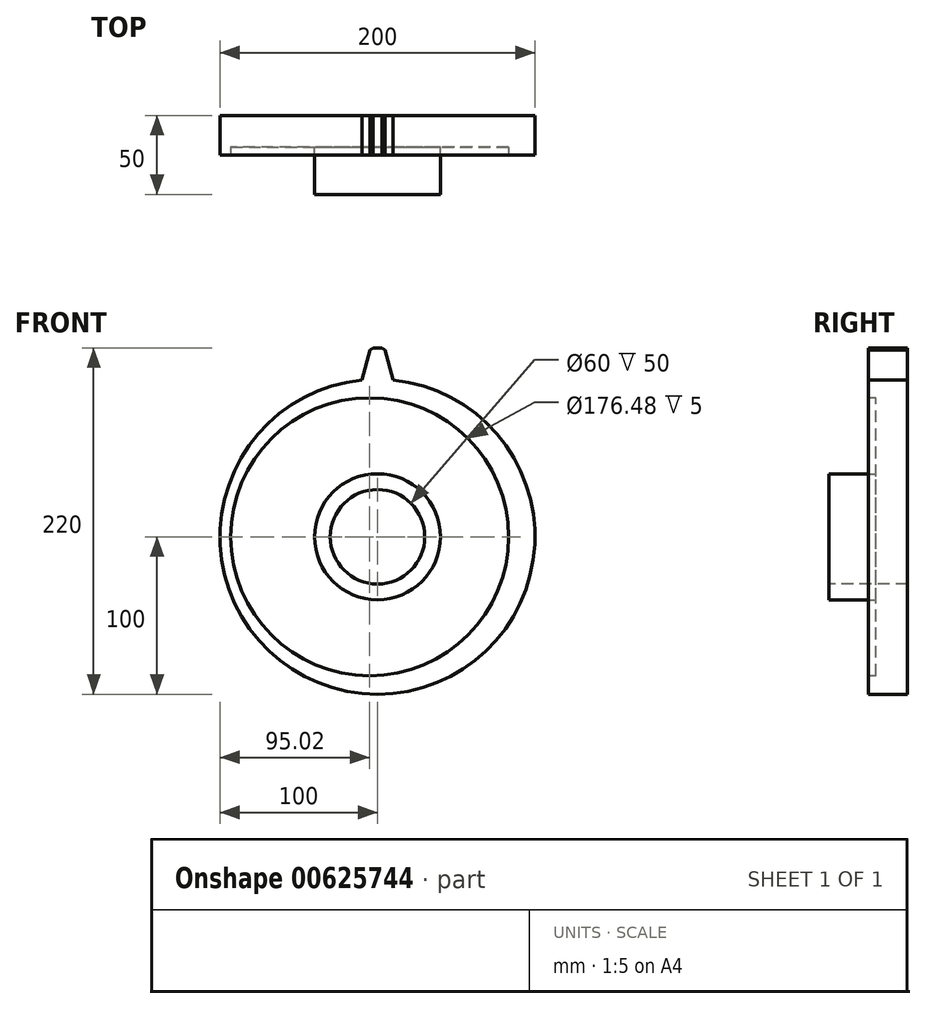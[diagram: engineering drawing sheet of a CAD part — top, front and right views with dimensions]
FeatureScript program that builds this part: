
annotation { "Feature Type Name" : "Feature", "Feature Type Description" : "" }
export const myFeature = defineFeature(function(context is Context, id is Id, definition is map)
    precondition{}
    {
        {
            var Q0;
            Q0=qCreatedBy(makeId("Front.planeOp"),FACE);
            var sketch = newSketch(context, id + "F0", { "sketchPlane" : qUnion([Q0])});
            skCircle(sketch, "E0", {"center": v(0, 0) * mm, "radius": 100 * mm});
            skSolve(sketch);
        }
        {
            var Q0;
            Q0 = qSketchRegion(id + "F0", true);
            extrude(context, id + "F1", {"entities" : qUnion([Q0]), "depth" : 25 * mm, "offsetDistance" : 25 * mm});
        }
        {
            var Q0;
            Q0=makeQuery(id+"F1.opExtrude","CAP_FACE",FACE,{"disambiguationData":[OSD([sQuery(id+"F0.wireOp",EDGE,"E0")])],"isStart":false});
            var sketch = newSketch(context, id + "F2", { "sketchPlane" : qUnion([Q0])});
            skLineSegment(sketch, "E1", {"start": v(-4.5, 120) * mm, "end": v(4.5, 120) * mm});
            skLineSegment(sketch, "E2", {"start": v(4.5, 120) * mm, "end": v(10, 99.5) * mm});
            skLineSegment(sketch, "E3", {"start": v(-4.5, 120) * mm, "end": v(-10, 99.5) * mm});
            skLineSegment(sketch, "E4", {"start": v(10, 99.5) * mm, "end": v(-10, 99.5) * mm});
            skSolve(sketch);
        }
        {
            var Q0;
            Q0 = qSketchRegion(id + "F2", true);
            extrude(context, id + "F3", {"entities" : qUnion([Q0]), "operationType" : NewBodyOperationType.ADD, "oppositeDirection" : true, "depth" : 25 * mm, "offsetDistance" : 25 * mm});
        }
        {
            var Q0;
            Q0=makeQuery(id+"F3.opExtrude","SWEPT_EDGE",EDGE,{"disambiguationData":[OSD([sQuery(id+"F2.wireOp",EDGE,"E1"),sQuery(id+"F2.wireOp",EDGE,"E2")])]});
            var Q1;
            Q1=makeQuery(id+"F3.opExtrude","SWEPT_EDGE",EDGE,{"disambiguationData":[OSD([sQuery(id+"F2.wireOp",EDGE,"E1"),sQuery(id+"F2.wireOp",EDGE,"E3")])]});
            chamfer(context, id + "F4", {"entities" : qUnion([Q0, Q1]), "width" : 2 * mm, "tangentPropagation" : true});
        }
        {
            var Q0;
            Q0=makeQuery(id+"F3.opExtrude","SWEPT_EDGE",EDGE,{"disambiguationData":[OSD([sQuery(id+"F0.wireOp",EDGE,"E0"),sQuery(id+"F2.wireOp",EDGE,"E2"),sQuery(id+"F2.wireOp",EDGE,"E4")])]});
            var Q1;
            Q1=makeQuery(id+"F3.opExtrude","SWEPT_EDGE",EDGE,{"disambiguationData":[OSD([sQuery(id+"F0.wireOp",EDGE,"E0"),sQuery(id+"F2.wireOp",EDGE,"E3"),sQuery(id+"F2.wireOp",EDGE,"E4")])]});
            fillet(context, id + "F5", {"entities" : qUnion([Q0, Q1]), "radius" : 5 * mm, "tangentPropagation" : true, "allowEdgeOverflow" : false});
        }
        {
            var Q0;
            {var subQ0=sQuery(id+"F2.wireOp",EDGE,"E4");var subQ1=sQuery(id+"F2.wireOp",EDGE,"E3");var subQ2=sQuery(id+"F2.wireOp",EDGE,"E2");var subQ3=sQuery(id+"F2.wireOp",EDGE,"E1");Q0=makeQuery(id+"FP0gZP2htBhd3En_1.19.F3.boolean.opBoolean","MERGE",FACE,{"derivedFrom":[makeQuery(id+"FP0gZP2htBhd3En_1.18.F3.boolean.opBoolean","MERGE",FACE,{"derivedFrom":[makeQuery(id+"FP0gZP2htBhd3En_1.17.F3.boolean.opBoolean","MERGE",FACE,{"derivedFrom":[makeQuery(id+"FP0gZP2htBhd3En_1.16.F3.boolean.opBoolean","MERGE",FACE,{"derivedFrom":[makeQuery(id+"FP0gZP2htBhd3En_1.15.F3.boolean.opBoolean","MERGE",FACE,{"derivedFrom":[makeQuery(id+"FP0gZP2htBhd3En_1.14.F3.boolean.opBoolean","MERGE",FACE,{"derivedFrom":[makeQuery(id+"FP0gZP2htBhd3En_1.13.F3.boolean.opBoolean","MERGE",FACE,{"derivedFrom":[makeQuery(id+"FP0gZP2htBhd3En_1.12.F3.boolean.opBoolean","MERGE",FACE,{"derivedFrom":[makeQuery(id+"FP0gZP2htBhd3En_1.11.F3.boolean.opBoolean","MERGE",FACE,{"derivedFrom":[makeQuery(id+"FP0gZP2htBhd3En_1.10.F3.boolean.opBoolean","MERGE",FACE,{"derivedFrom":[makeQuery(id+"FP0gZP2htBhd3En_1.9.F3.boolean.opBoolean","MERGE",FACE,{"derivedFrom":[makeQuery(id+"FP0gZP2htBhd3En_1.8.F3.boolean.opBoolean","MERGE",FACE,{"derivedFrom":[makeQuery(id+"FP0gZP2htBhd3En_1.7.F3.boolean.opBoolean","MERGE",FACE,{"derivedFrom":[makeQuery(id+"FP0gZP2htBhd3En_1.6.F3.boolean.opBoolean","MERGE",FACE,{"derivedFrom":[makeQuery(id+"FP0gZP2htBhd3En_1.5.F3.boolean.opBoolean","MERGE",FACE,{"derivedFrom":[makeQuery(id+"FP0gZP2htBhd3En_1.4.F3.boolean.opBoolean","MERGE",FACE,{"derivedFrom":[makeQuery(id+"FP0gZP2htBhd3En_1.3.F3.boolean.opBoolean","MERGE",FACE,{"derivedFrom":[makeQuery(id+"FP0gZP2htBhd3En_1.2.F3.boolean.opBoolean","MERGE",FACE,{"derivedFrom":[makeQuery(id+"FP0gZP2htBhd3En_1.1.F3.boolean.opBoolean","MERGE",FACE,{"derivedFrom":[makeQuery(id+"F3.boolean.opBoolean","MERGE",FACE,{"derivedFrom":[makeQuery(id+"F1.opExtrude","CAP_FACE",FACE,{"disambiguationData":[OSD([sQuery(id+"F0.wireOp",EDGE,"E0")])],"isStart":false}),makeQuery(id+"F3.opExtrude","CAP_FACE",FACE,{"disambiguationData":[OSD([subQ3,subQ2,subQ1,subQ0])],"isStart":true})]}),makeQuery(id+"FP0gZP2htBhd3En_1.1.F3.opExtrude","CAP_FACE",FACE,{"disambiguationData":[OSD([subQ3,subQ2,subQ1,subQ0])],"isStart":true})]}),makeQuery(id+"FP0gZP2htBhd3En_1.2.F3.opExtrude","CAP_FACE",FACE,{"disambiguationData":[OSD([subQ3,subQ2,subQ1,subQ0])],"isStart":true})]}),makeQuery(id+"FP0gZP2htBhd3En_1.3.F3.opExtrude","CAP_FACE",FACE,{"disambiguationData":[OSD([subQ3,subQ2,subQ1,subQ0])],"isStart":true})]}),makeQuery(id+"FP0gZP2htBhd3En_1.4.F3.opExtrude","CAP_FACE",FACE,{"disambiguationData":[OSD([subQ3,subQ2,subQ1,subQ0])],"isStart":true})]}),makeQuery(id+"FP0gZP2htBhd3En_1.5.F3.opExtrude","CAP_FACE",FACE,{"disambiguationData":[OSD([subQ3,subQ2,subQ1,subQ0])],"isStart":true})]}),makeQuery(id+"FP0gZP2htBhd3En_1.6.F3.opExtrude","CAP_FACE",FACE,{"disambiguationData":[OSD([subQ3,subQ2,subQ1,subQ0])],"isStart":true})]}),makeQuery(id+"FP0gZP2htBhd3En_1.7.F3.opExtrude","CAP_FACE",FACE,{"disambiguationData":[OSD([subQ3,subQ2,subQ1,subQ0])],"isStart":true})]}),makeQuery(id+"FP0gZP2htBhd3En_1.8.F3.opExtrude","CAP_FACE",FACE,{"disambiguationData":[OSD([subQ3,subQ2,subQ1,subQ0])],"isStart":true})]}),makeQuery(id+"FP0gZP2htBhd3En_1.9.F3.opExtrude","CAP_FACE",FACE,{"disambiguationData":[OSD([subQ3,subQ2,subQ1,subQ0])],"isStart":true})]}),makeQuery(id+"FP0gZP2htBhd3En_1.10.F3.opExtrude","CAP_FACE",FACE,{"disambiguationData":[OSD([subQ3,subQ2,subQ1,subQ0])],"isStart":true})]}),makeQuery(id+"FP0gZP2htBhd3En_1.11.F3.opExtrude","CAP_FACE",FACE,{"disambiguationData":[OSD([subQ3,subQ2,subQ1,subQ0])],"isStart":true})]}),makeQuery(id+"FP0gZP2htBhd3En_1.12.F3.opExtrude","CAP_FACE",FACE,{"disambiguationData":[OSD([subQ3,subQ2,subQ1,subQ0])],"isStart":true})]}),makeQuery(id+"FP0gZP2htBhd3En_1.13.F3.opExtrude","CAP_FACE",FACE,{"disambiguationData":[OSD([subQ3,subQ2,subQ1,subQ0])],"isStart":true})]}),makeQuery(id+"FP0gZP2htBhd3En_1.14.F3.opExtrude","CAP_FACE",FACE,{"disambiguationData":[OSD([subQ3,subQ2,subQ1,subQ0])],"isStart":true})]}),makeQuery(id+"FP0gZP2htBhd3En_1.15.F3.opExtrude","CAP_FACE",FACE,{"disambiguationData":[OSD([subQ3,subQ2,subQ1,subQ0])],"isStart":true})]}),makeQuery(id+"FP0gZP2htBhd3En_1.16.F3.opExtrude","CAP_FACE",FACE,{"disambiguationData":[OSD([subQ3,subQ2,subQ1,subQ0])],"isStart":true})]}),makeQuery(id+"FP0gZP2htBhd3En_1.17.F3.opExtrude","CAP_FACE",FACE,{"disambiguationData":[OSD([subQ3,subQ2,subQ1,subQ0])],"isStart":true})]}),makeQuery(id+"FP0gZP2htBhd3En_1.18.F3.opExtrude","CAP_FACE",FACE,{"disambiguationData":[OSD([subQ3,subQ2,subQ1,subQ0])],"isStart":true})]}),makeQuery(id+"FP0gZP2htBhd3En_1.19.F3.opExtrude","CAP_FACE",FACE,{"disambiguationData":[OSD([subQ3,subQ2,subQ1,subQ0])],"isStart":true})]});}
            var sketch = newSketch(context, id + "F6", { "sketchPlane" : qUnion([Q0])});
            skCircle(sketch, "E5", {"center": v(0, 0) * mm, "radius": 90 * mm});
            skCircle(sketch, "E6", {"center": v(0, 0) * mm, "radius": 30 * mm});
            skSolve(sketch);
        }
        {
            var Q0;
            Q0=makeQuery(id+"F6.imprint","IMPRINT",FACE,{"disambiguationData":[TD([[makeQuery(id+"F6.imprint","IMPRINT",EDGE,{"derivedFrom":sQuery(id+"F6.wireOp",EDGE,"E6")}),1.0]])]});
            extrude(context, id + "F7", {"entities" : qUnion([Q0]), "operationType" : NewBodyOperationType.REMOVE, "oppositeDirection" : true, "depth" : 25 * mm, "offsetDistance" : 25 * mm});
        }
        {
            var Q0;
            {var subQ0=sQuery(id+"F2.wireOp",EDGE,"E4");var subQ1=sQuery(id+"F2.wireOp",EDGE,"E3");var subQ2=sQuery(id+"F2.wireOp",EDGE,"E2");var subQ3=sQuery(id+"F2.wireOp",EDGE,"E1");Q0=makeQuery(id+"FP0gZP2htBhd3En_1.19.F3.boolean.opBoolean","MERGE",FACE,{"derivedFrom":[makeQuery(id+"FP0gZP2htBhd3En_1.18.F3.boolean.opBoolean","MERGE",FACE,{"derivedFrom":[makeQuery(id+"FP0gZP2htBhd3En_1.17.F3.boolean.opBoolean","MERGE",FACE,{"derivedFrom":[makeQuery(id+"FP0gZP2htBhd3En_1.16.F3.boolean.opBoolean","MERGE",FACE,{"derivedFrom":[makeQuery(id+"FP0gZP2htBhd3En_1.15.F3.boolean.opBoolean","MERGE",FACE,{"derivedFrom":[makeQuery(id+"FP0gZP2htBhd3En_1.14.F3.boolean.opBoolean","MERGE",FACE,{"derivedFrom":[makeQuery(id+"FP0gZP2htBhd3En_1.13.F3.boolean.opBoolean","MERGE",FACE,{"derivedFrom":[makeQuery(id+"FP0gZP2htBhd3En_1.12.F3.boolean.opBoolean","MERGE",FACE,{"derivedFrom":[makeQuery(id+"FP0gZP2htBhd3En_1.11.F3.boolean.opBoolean","MERGE",FACE,{"derivedFrom":[makeQuery(id+"FP0gZP2htBhd3En_1.10.F3.boolean.opBoolean","MERGE",FACE,{"derivedFrom":[makeQuery(id+"FP0gZP2htBhd3En_1.9.F3.boolean.opBoolean","MERGE",FACE,{"derivedFrom":[makeQuery(id+"FP0gZP2htBhd3En_1.8.F3.boolean.opBoolean","MERGE",FACE,{"derivedFrom":[makeQuery(id+"FP0gZP2htBhd3En_1.7.F3.boolean.opBoolean","MERGE",FACE,{"derivedFrom":[makeQuery(id+"FP0gZP2htBhd3En_1.6.F3.boolean.opBoolean","MERGE",FACE,{"derivedFrom":[makeQuery(id+"FP0gZP2htBhd3En_1.5.F3.boolean.opBoolean","MERGE",FACE,{"derivedFrom":[makeQuery(id+"FP0gZP2htBhd3En_1.4.F3.boolean.opBoolean","MERGE",FACE,{"derivedFrom":[makeQuery(id+"FP0gZP2htBhd3En_1.3.F3.boolean.opBoolean","MERGE",FACE,{"derivedFrom":[makeQuery(id+"FP0gZP2htBhd3En_1.2.F3.boolean.opBoolean","MERGE",FACE,{"derivedFrom":[makeQuery(id+"FP0gZP2htBhd3En_1.1.F3.boolean.opBoolean","MERGE",FACE,{"derivedFrom":[makeQuery(id+"F3.boolean.opBoolean","MERGE",FACE,{"derivedFrom":[makeQuery(id+"F1.opExtrude","CAP_FACE",FACE,{"disambiguationData":[OSD([sQuery(id+"F0.wireOp",EDGE,"E0")])],"isStart":true}),makeQuery(id+"F3.opExtrude","CAP_FACE",FACE,{"disambiguationData":[OSD([subQ3,subQ2,subQ1,subQ0])],"isStart":false})]}),makeQuery(id+"FP0gZP2htBhd3En_1.1.F3.opExtrude","CAP_FACE",FACE,{"disambiguationData":[OSD([subQ3,subQ2,subQ1,subQ0])],"isStart":false})]}),makeQuery(id+"FP0gZP2htBhd3En_1.2.F3.opExtrude","CAP_FACE",FACE,{"disambiguationData":[OSD([subQ3,subQ2,subQ1,subQ0])],"isStart":false})]}),makeQuery(id+"FP0gZP2htBhd3En_1.3.F3.opExtrude","CAP_FACE",FACE,{"disambiguationData":[OSD([subQ3,subQ2,subQ1,subQ0])],"isStart":false})]}),makeQuery(id+"FP0gZP2htBhd3En_1.4.F3.opExtrude","CAP_FACE",FACE,{"disambiguationData":[OSD([subQ3,subQ2,subQ1,subQ0])],"isStart":false})]}),makeQuery(id+"FP0gZP2htBhd3En_1.5.F3.opExtrude","CAP_FACE",FACE,{"disambiguationData":[OSD([subQ3,subQ2,subQ1,subQ0])],"isStart":false})]}),makeQuery(id+"FP0gZP2htBhd3En_1.6.F3.opExtrude","CAP_FACE",FACE,{"disambiguationData":[OSD([subQ3,subQ2,subQ1,subQ0])],"isStart":false})]}),makeQuery(id+"FP0gZP2htBhd3En_1.7.F3.opExtrude","CAP_FACE",FACE,{"disambiguationData":[OSD([subQ3,subQ2,subQ1,subQ0])],"isStart":false})]}),makeQuery(id+"FP0gZP2htBhd3En_1.8.F3.opExtrude","CAP_FACE",FACE,{"disambiguationData":[OSD([subQ3,subQ2,subQ1,subQ0])],"isStart":false})]}),makeQuery(id+"FP0gZP2htBhd3En_1.9.F3.opExtrude","CAP_FACE",FACE,{"disambiguationData":[OSD([subQ3,subQ2,subQ1,subQ0])],"isStart":false})]}),makeQuery(id+"FP0gZP2htBhd3En_1.10.F3.opExtrude","CAP_FACE",FACE,{"disambiguationData":[OSD([subQ3,subQ2,subQ1,subQ0])],"isStart":false})]}),makeQuery(id+"FP0gZP2htBhd3En_1.11.F3.opExtrude","CAP_FACE",FACE,{"disambiguationData":[OSD([subQ3,subQ2,subQ1,subQ0])],"isStart":false})]}),makeQuery(id+"FP0gZP2htBhd3En_1.12.F3.opExtrude","CAP_FACE",FACE,{"disambiguationData":[OSD([subQ3,subQ2,subQ1,subQ0])],"isStart":false})]}),makeQuery(id+"FP0gZP2htBhd3En_1.13.F3.opExtrude","CAP_FACE",FACE,{"disambiguationData":[OSD([subQ3,subQ2,subQ1,subQ0])],"isStart":false})]}),makeQuery(id+"FP0gZP2htBhd3En_1.14.F3.opExtrude","CAP_FACE",FACE,{"disambiguationData":[OSD([subQ3,subQ2,subQ1,subQ0])],"isStart":false})]}),makeQuery(id+"FP0gZP2htBhd3En_1.15.F3.opExtrude","CAP_FACE",FACE,{"disambiguationData":[OSD([subQ3,subQ2,subQ1,subQ0])],"isStart":false})]}),makeQuery(id+"FP0gZP2htBhd3En_1.16.F3.opExtrude","CAP_FACE",FACE,{"disambiguationData":[OSD([subQ3,subQ2,subQ1,subQ0])],"isStart":false})]}),makeQuery(id+"FP0gZP2htBhd3En_1.17.F3.opExtrude","CAP_FACE",FACE,{"disambiguationData":[OSD([subQ3,subQ2,subQ1,subQ0])],"isStart":false})]}),makeQuery(id+"FP0gZP2htBhd3En_1.18.F3.opExtrude","CAP_FACE",FACE,{"disambiguationData":[OSD([subQ3,subQ2,subQ1,subQ0])],"isStart":false})]}),makeQuery(id+"FP0gZP2htBhd3En_1.19.F3.opExtrude","CAP_FACE",FACE,{"disambiguationData":[OSD([subQ3,subQ2,subQ1,subQ0])],"isStart":false})]});}
            var sketch = newSketch(context, id + "F8", { "sketchPlane" : qUnion([Q0])});
            skCircle(sketch, "E7", {"center": v(0, 0) * mm, "radius": 90 * mm});
            skSolve(sketch);
        }
        {
            var Q0;
            {var subQ0=sQuery(id+"F2.wireOp",EDGE,"E4");var subQ1=sQuery(id+"F2.wireOp",EDGE,"E3");var subQ2=sQuery(id+"F2.wireOp",EDGE,"E2");var subQ3=sQuery(id+"F2.wireOp",EDGE,"E1");Q0=makeQuery(id+"FP0gZP2htBhd3En_1.19.F3.boolean.opBoolean","MERGE",FACE,{"derivedFrom":[makeQuery(id+"FP0gZP2htBhd3En_1.18.F3.boolean.opBoolean","MERGE",FACE,{"derivedFrom":[makeQuery(id+"FP0gZP2htBhd3En_1.17.F3.boolean.opBoolean","MERGE",FACE,{"derivedFrom":[makeQuery(id+"FP0gZP2htBhd3En_1.16.F3.boolean.opBoolean","MERGE",FACE,{"derivedFrom":[makeQuery(id+"FP0gZP2htBhd3En_1.15.F3.boolean.opBoolean","MERGE",FACE,{"derivedFrom":[makeQuery(id+"FP0gZP2htBhd3En_1.14.F3.boolean.opBoolean","MERGE",FACE,{"derivedFrom":[makeQuery(id+"FP0gZP2htBhd3En_1.13.F3.boolean.opBoolean","MERGE",FACE,{"derivedFrom":[makeQuery(id+"FP0gZP2htBhd3En_1.12.F3.boolean.opBoolean","MERGE",FACE,{"derivedFrom":[makeQuery(id+"FP0gZP2htBhd3En_1.11.F3.boolean.opBoolean","MERGE",FACE,{"derivedFrom":[makeQuery(id+"FP0gZP2htBhd3En_1.10.F3.boolean.opBoolean","MERGE",FACE,{"derivedFrom":[makeQuery(id+"FP0gZP2htBhd3En_1.9.F3.boolean.opBoolean","MERGE",FACE,{"derivedFrom":[makeQuery(id+"FP0gZP2htBhd3En_1.8.F3.boolean.opBoolean","MERGE",FACE,{"derivedFrom":[makeQuery(id+"FP0gZP2htBhd3En_1.7.F3.boolean.opBoolean","MERGE",FACE,{"derivedFrom":[makeQuery(id+"FP0gZP2htBhd3En_1.6.F3.boolean.opBoolean","MERGE",FACE,{"derivedFrom":[makeQuery(id+"FP0gZP2htBhd3En_1.5.F3.boolean.opBoolean","MERGE",FACE,{"derivedFrom":[makeQuery(id+"FP0gZP2htBhd3En_1.4.F3.boolean.opBoolean","MERGE",FACE,{"derivedFrom":[makeQuery(id+"FP0gZP2htBhd3En_1.3.F3.boolean.opBoolean","MERGE",FACE,{"derivedFrom":[makeQuery(id+"FP0gZP2htBhd3En_1.2.F3.boolean.opBoolean","MERGE",FACE,{"derivedFrom":[makeQuery(id+"FP0gZP2htBhd3En_1.1.F3.boolean.opBoolean","MERGE",FACE,{"derivedFrom":[makeQuery(id+"F3.boolean.opBoolean","MERGE",FACE,{"derivedFrom":[makeQuery(id+"F1.opExtrude","CAP_FACE",FACE,{"disambiguationData":[OSD([sQuery(id+"F0.wireOp",EDGE,"E0")])],"isStart":false}),makeQuery(id+"F3.opExtrude","CAP_FACE",FACE,{"disambiguationData":[OSD([subQ3,subQ2,subQ1,subQ0])],"isStart":true})]}),makeQuery(id+"FP0gZP2htBhd3En_1.1.F3.opExtrude","CAP_FACE",FACE,{"disambiguationData":[OSD([subQ3,subQ2,subQ1,subQ0])],"isStart":true})]}),makeQuery(id+"FP0gZP2htBhd3En_1.2.F3.opExtrude","CAP_FACE",FACE,{"disambiguationData":[OSD([subQ3,subQ2,subQ1,subQ0])],"isStart":true})]}),makeQuery(id+"FP0gZP2htBhd3En_1.3.F3.opExtrude","CAP_FACE",FACE,{"disambiguationData":[OSD([subQ3,subQ2,subQ1,subQ0])],"isStart":true})]}),makeQuery(id+"FP0gZP2htBhd3En_1.4.F3.opExtrude","CAP_FACE",FACE,{"disambiguationData":[OSD([subQ3,subQ2,subQ1,subQ0])],"isStart":true})]}),makeQuery(id+"FP0gZP2htBhd3En_1.5.F3.opExtrude","CAP_FACE",FACE,{"disambiguationData":[OSD([subQ3,subQ2,subQ1,subQ0])],"isStart":true})]}),makeQuery(id+"FP0gZP2htBhd3En_1.6.F3.opExtrude","CAP_FACE",FACE,{"disambiguationData":[OSD([subQ3,subQ2,subQ1,subQ0])],"isStart":true})]}),makeQuery(id+"FP0gZP2htBhd3En_1.7.F3.opExtrude","CAP_FACE",FACE,{"disambiguationData":[OSD([subQ3,subQ2,subQ1,subQ0])],"isStart":true})]}),makeQuery(id+"FP0gZP2htBhd3En_1.8.F3.opExtrude","CAP_FACE",FACE,{"disambiguationData":[OSD([subQ3,subQ2,subQ1,subQ0])],"isStart":true})]}),makeQuery(id+"FP0gZP2htBhd3En_1.9.F3.opExtrude","CAP_FACE",FACE,{"disambiguationData":[OSD([subQ3,subQ2,subQ1,subQ0])],"isStart":true})]}),makeQuery(id+"FP0gZP2htBhd3En_1.10.F3.opExtrude","CAP_FACE",FACE,{"disambiguationData":[OSD([subQ3,subQ2,subQ1,subQ0])],"isStart":true})]}),makeQuery(id+"FP0gZP2htBhd3En_1.11.F3.opExtrude","CAP_FACE",FACE,{"disambiguationData":[OSD([subQ3,subQ2,subQ1,subQ0])],"isStart":true})]}),makeQuery(id+"FP0gZP2htBhd3En_1.12.F3.opExtrude","CAP_FACE",FACE,{"disambiguationData":[OSD([subQ3,subQ2,subQ1,subQ0])],"isStart":true})]}),makeQuery(id+"FP0gZP2htBhd3En_1.13.F3.opExtrude","CAP_FACE",FACE,{"disambiguationData":[OSD([subQ3,subQ2,subQ1,subQ0])],"isStart":true})]}),makeQuery(id+"FP0gZP2htBhd3En_1.14.F3.opExtrude","CAP_FACE",FACE,{"disambiguationData":[OSD([subQ3,subQ2,subQ1,subQ0])],"isStart":true})]}),makeQuery(id+"FP0gZP2htBhd3En_1.15.F3.opExtrude","CAP_FACE",FACE,{"disambiguationData":[OSD([subQ3,subQ2,subQ1,subQ0])],"isStart":true})]}),makeQuery(id+"FP0gZP2htBhd3En_1.16.F3.opExtrude","CAP_FACE",FACE,{"disambiguationData":[OSD([subQ3,subQ2,subQ1,subQ0])],"isStart":true})]}),makeQuery(id+"FP0gZP2htBhd3En_1.17.F3.opExtrude","CAP_FACE",FACE,{"disambiguationData":[OSD([subQ3,subQ2,subQ1,subQ0])],"isStart":true})]}),makeQuery(id+"FP0gZP2htBhd3En_1.18.F3.opExtrude","CAP_FACE",FACE,{"disambiguationData":[OSD([subQ3,subQ2,subQ1,subQ0])],"isStart":true})]}),makeQuery(id+"FP0gZP2htBhd3En_1.19.F3.opExtrude","CAP_FACE",FACE,{"disambiguationData":[OSD([subQ3,subQ2,subQ1,subQ0])],"isStart":true})]});}
            var sketch = newSketch(context, id + "F9", { "sketchPlane" : qUnion([Q0])});
            skCircle(sketch, "E8", {"center": v(0, 0) * mm, "radius": 40 * mm});
            skSolve(sketch);
        }
        {
            var Q0;
            Q0=makeQuery(id+"F9.imprint","IMPRINT",FACE,{"disambiguationData":[TD([[makeQuery(id+"F9.imprint","IMPRINT",EDGE,{"derivedFrom":sQuery(id+"F9.wireOp",EDGE,"E8")}),1.0]])]});
            extrude(context, id + "F10", {"entities" : qUnion([Q0]), "operationType" : NewBodyOperationType.ADD, "depth" : 25 * mm, "offsetDistance" : 25 * mm});
        }
        {
            var Q0;
            {var subQ0=sQuery(id+"F2.wireOp",EDGE,"E4");var subQ1=sQuery(id+"F2.wireOp",EDGE,"E3");var subQ2=sQuery(id+"F2.wireOp",EDGE,"E2");var subQ3=sQuery(id+"F2.wireOp",EDGE,"E1");Q0=makeQuery(id+"FP0gZP2htBhd3En_1.19.F3.boolean.opBoolean","MERGE",FACE,{"derivedFrom":[makeQuery(id+"FP0gZP2htBhd3En_1.18.F3.boolean.opBoolean","MERGE",FACE,{"derivedFrom":[makeQuery(id+"FP0gZP2htBhd3En_1.17.F3.boolean.opBoolean","MERGE",FACE,{"derivedFrom":[makeQuery(id+"FP0gZP2htBhd3En_1.16.F3.boolean.opBoolean","MERGE",FACE,{"derivedFrom":[makeQuery(id+"FP0gZP2htBhd3En_1.15.F3.boolean.opBoolean","MERGE",FACE,{"derivedFrom":[makeQuery(id+"FP0gZP2htBhd3En_1.14.F3.boolean.opBoolean","MERGE",FACE,{"derivedFrom":[makeQuery(id+"FP0gZP2htBhd3En_1.13.F3.boolean.opBoolean","MERGE",FACE,{"derivedFrom":[makeQuery(id+"FP0gZP2htBhd3En_1.12.F3.boolean.opBoolean","MERGE",FACE,{"derivedFrom":[makeQuery(id+"FP0gZP2htBhd3En_1.11.F3.boolean.opBoolean","MERGE",FACE,{"derivedFrom":[makeQuery(id+"FP0gZP2htBhd3En_1.10.F3.boolean.opBoolean","MERGE",FACE,{"derivedFrom":[makeQuery(id+"FP0gZP2htBhd3En_1.9.F3.boolean.opBoolean","MERGE",FACE,{"derivedFrom":[makeQuery(id+"FP0gZP2htBhd3En_1.8.F3.boolean.opBoolean","MERGE",FACE,{"derivedFrom":[makeQuery(id+"FP0gZP2htBhd3En_1.7.F3.boolean.opBoolean","MERGE",FACE,{"derivedFrom":[makeQuery(id+"FP0gZP2htBhd3En_1.6.F3.boolean.opBoolean","MERGE",FACE,{"derivedFrom":[makeQuery(id+"FP0gZP2htBhd3En_1.5.F3.boolean.opBoolean","MERGE",FACE,{"derivedFrom":[makeQuery(id+"FP0gZP2htBhd3En_1.4.F3.boolean.opBoolean","MERGE",FACE,{"derivedFrom":[makeQuery(id+"FP0gZP2htBhd3En_1.3.F3.boolean.opBoolean","MERGE",FACE,{"derivedFrom":[makeQuery(id+"FP0gZP2htBhd3En_1.2.F3.boolean.opBoolean","MERGE",FACE,{"derivedFrom":[makeQuery(id+"FP0gZP2htBhd3En_1.1.F3.boolean.opBoolean","MERGE",FACE,{"derivedFrom":[makeQuery(id+"F3.boolean.opBoolean","MERGE",FACE,{"derivedFrom":[makeQuery(id+"F1.opExtrude","CAP_FACE",FACE,{"disambiguationData":[OSD([sQuery(id+"F0.wireOp",EDGE,"E0")])],"isStart":false}),makeQuery(id+"F3.opExtrude","CAP_FACE",FACE,{"disambiguationData":[OSD([subQ3,subQ2,subQ1,subQ0])],"isStart":true})]}),makeQuery(id+"FP0gZP2htBhd3En_1.1.F3.opExtrude","CAP_FACE",FACE,{"disambiguationData":[OSD([subQ3,subQ2,subQ1,subQ0])],"isStart":true})]}),makeQuery(id+"FP0gZP2htBhd3En_1.2.F3.opExtrude","CAP_FACE",FACE,{"disambiguationData":[OSD([subQ3,subQ2,subQ1,subQ0])],"isStart":true})]}),makeQuery(id+"FP0gZP2htBhd3En_1.3.F3.opExtrude","CAP_FACE",FACE,{"disambiguationData":[OSD([subQ3,subQ2,subQ1,subQ0])],"isStart":true})]}),makeQuery(id+"FP0gZP2htBhd3En_1.4.F3.opExtrude","CAP_FACE",FACE,{"disambiguationData":[OSD([subQ3,subQ2,subQ1,subQ0])],"isStart":true})]}),makeQuery(id+"FP0gZP2htBhd3En_1.5.F3.opExtrude","CAP_FACE",FACE,{"disambiguationData":[OSD([subQ3,subQ2,subQ1,subQ0])],"isStart":true})]}),makeQuery(id+"FP0gZP2htBhd3En_1.6.F3.opExtrude","CAP_FACE",FACE,{"disambiguationData":[OSD([subQ3,subQ2,subQ1,subQ0])],"isStart":true})]}),makeQuery(id+"FP0gZP2htBhd3En_1.7.F3.opExtrude","CAP_FACE",FACE,{"disambiguationData":[OSD([subQ3,subQ2,subQ1,subQ0])],"isStart":true})]}),makeQuery(id+"FP0gZP2htBhd3En_1.8.F3.opExtrude","CAP_FACE",FACE,{"disambiguationData":[OSD([subQ3,subQ2,subQ1,subQ0])],"isStart":true})]}),makeQuery(id+"FP0gZP2htBhd3En_1.9.F3.opExtrude","CAP_FACE",FACE,{"disambiguationData":[OSD([subQ3,subQ2,subQ1,subQ0])],"isStart":true})]}),makeQuery(id+"FP0gZP2htBhd3En_1.10.F3.opExtrude","CAP_FACE",FACE,{"disambiguationData":[OSD([subQ3,subQ2,subQ1,subQ0])],"isStart":true})]}),makeQuery(id+"FP0gZP2htBhd3En_1.11.F3.opExtrude","CAP_FACE",FACE,{"disambiguationData":[OSD([subQ3,subQ2,subQ1,subQ0])],"isStart":true})]}),makeQuery(id+"FP0gZP2htBhd3En_1.12.F3.opExtrude","CAP_FACE",FACE,{"disambiguationData":[OSD([subQ3,subQ2,subQ1,subQ0])],"isStart":true})]}),makeQuery(id+"FP0gZP2htBhd3En_1.13.F3.opExtrude","CAP_FACE",FACE,{"disambiguationData":[OSD([subQ3,subQ2,subQ1,subQ0])],"isStart":true})]}),makeQuery(id+"FP0gZP2htBhd3En_1.14.F3.opExtrude","CAP_FACE",FACE,{"disambiguationData":[OSD([subQ3,subQ2,subQ1,subQ0])],"isStart":true})]}),makeQuery(id+"FP0gZP2htBhd3En_1.15.F3.opExtrude","CAP_FACE",FACE,{"disambiguationData":[OSD([subQ3,subQ2,subQ1,subQ0])],"isStart":true})]}),makeQuery(id+"FP0gZP2htBhd3En_1.16.F3.opExtrude","CAP_FACE",FACE,{"disambiguationData":[OSD([subQ3,subQ2,subQ1,subQ0])],"isStart":true})]}),makeQuery(id+"FP0gZP2htBhd3En_1.17.F3.opExtrude","CAP_FACE",FACE,{"disambiguationData":[OSD([subQ3,subQ2,subQ1,subQ0])],"isStart":true})]}),makeQuery(id+"FP0gZP2htBhd3En_1.18.F3.opExtrude","CAP_FACE",FACE,{"disambiguationData":[OSD([subQ3,subQ2,subQ1,subQ0])],"isStart":true})]}),makeQuery(id+"FP0gZP2htBhd3En_1.19.F3.opExtrude","CAP_FACE",FACE,{"disambiguationData":[OSD([subQ3,subQ2,subQ1,subQ0])],"isStart":true})]});}
            var sketch = newSketch(context, id + "F11", { "sketchPlane" : qUnion([Q0])});
            skCircle(sketch, "E9", {"center": v(-4.98, 0) * mm, "radius": 88.24 * mm});
            skSolve(sketch);
        }
        {
            var Q0;
            Q0=makeQuery(id+"F11.imprint","IMPRINT",FACE,{"disambiguationData":[TD([[makeQuery(id+"F11.imprint","IMPRINT",EDGE,{"derivedFrom":sQuery(id+"F11.wireOp",EDGE,"E9")}),1.0]])]});
            extrude(context, id + "F12", {"entities" : qUnion([Q0]), "operationType" : NewBodyOperationType.REMOVE, "oppositeDirection" : true, "depth" : 5 * mm, "offsetDistance" : 25 * mm});
        }
    });
